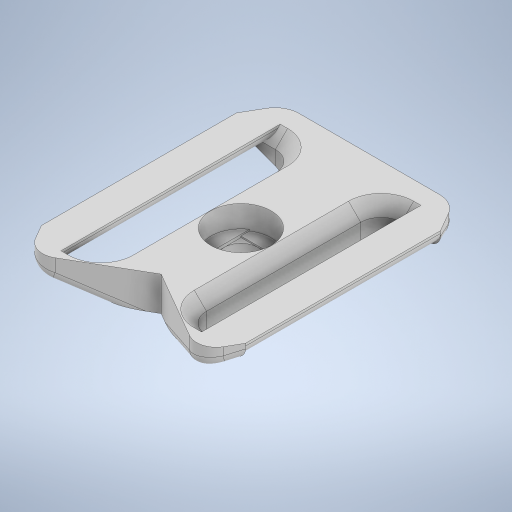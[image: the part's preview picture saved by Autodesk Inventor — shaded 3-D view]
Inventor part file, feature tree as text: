
AUTODESK INVENTOR PART (.ipt)
format: ipt  version: 2024 (Build 280153000, 153)  size: 567,808 bytes
history: native  units: in
note: dims shown in document units (in); Inventor stores cm internally (conversion verified against a paired STEP export)
features: extrude x8, chamfer x4, direct_edit x3, fillet x3, move_body x3, sketch x1
ambient origin geometry x8: Origin, YZ Plane, XZ Plane, XY Plane, X Axis, Y Axis, Z Axis, Center Point
bodies: Solid1 (feature_tree)
feature tree (22):
  sketch  "Sketch1"  dims[d2=0.1181in d3=0.0in d5=0.2677in d6=2.2146in d7=0.785in d8=0.4862in d12=0.7874in d18=0.315in d20=0.1575in d21=0.1575in d27=0.1969in d30=0.1575in d31=0.0in d37=0.3051in d38=0.3051in d44=0.0in d45=0.0in d46=0.0in d47=0.0in d48=-0.0591in d49=0.0591in d50=0.0in d51=0.0in d52=0.0in d53=0.0in d54=-0.0197in d55=0.0591in d56=0.0591in d57=0.0118in d58=0.0in d59=0.0236in d60=0.0in d61=0.0984in d62=0.0787in d63=45.0deg d64=0.0787in d65=0.2126in d67=0.1181in d68=0.3543in d69=0.0in d70=0.1884in d71=0.0787in d72=45.0deg d73=0.0492in d74=0.0787in d75=45.0deg d76=0.0787in d77=0.1181in d79=0.0394in d80=0.0in d81=-0.0394in d82=0.0in d86=0.1181in d87=0.0591in d88=0.0in d89=0.0591in d90=0.0787in d91=45.0deg d92=0.689in d26=0.0197in d28=0.0197in d29=0.0344in d41=0.0197in d42=0.0344in d43=0.0197in]
  extrude  "Extrusion1"  Depth=0.0787in
  extrude  "Extrusion5"  Depth=0.0787in
  extrude  "Extrusion7"  Depth=0.0787in
  direct_edit  "Direct Edit2"
  extrude  "Extrusion8"  Depth=0.0787in
  direct_edit  "Direct Edit3"
  extrude  "Extrusion9"  Depth=0.0787in
  extrude  "Extrusion10"  Depth=0.0787in
  chamfer  "Chamfer2"  Distance=0.1575in
  fillet  "Fillet1"  Radius=0.1575in
  extrude  "Extrusion11"  Depth=0.1969in
  chamfer  "Chamfer4"  Distance=0.1575in
  chamfer  "Chamfer3"  Distance=0.3051in
  fillet  "Fillet2"  Radius=0.3051in
  fillet  "Fillet3"  [1 undecoded]
  direct_edit  "Direct Edit4"
  extrude  "Extrusion13"  TaperAngle=0.0deg  [1 undecoded]
  chamfer  "Chamfer5"  Distance=0.0591in
  move_body  "Move2"
  move_body  "Move3"
  move_body  "Move4"
note: 2 required parameter values undecoded (feature->parameter linkage not recoverable at this tier; creation-order binding heuristic only, values carry confidence <= 0.55)
